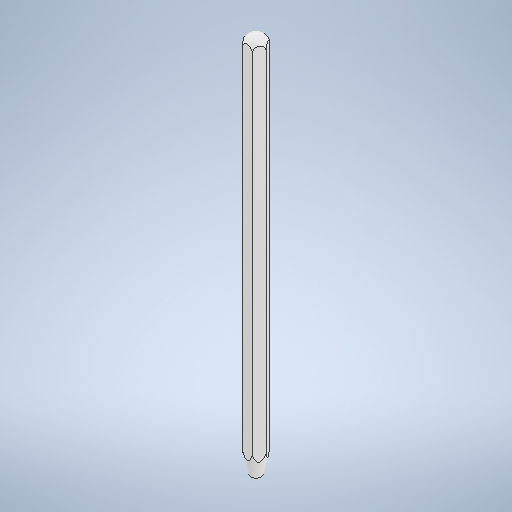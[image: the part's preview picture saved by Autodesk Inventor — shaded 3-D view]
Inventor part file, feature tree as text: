
AUTODESK INVENTOR PART (.ipt)
format: ipt  version: 2025.1 (Build 291241000, 241)  size: 307,200 bytes
history: native  units: mm
features: thicken_offset x6, sketch x5, revolve x3, extrude x2
ambient origin geometry x8: Origin, YZ Plane, XZ Plane, XY Plane, X Axis, Y Axis, Z Axis, Center Point
bodies: Solid1 (feature_tree)
feature tree (16):
  extrude  "Extrusion1"  Depth=155.0mm TaperAngle=0.0deg
  revolve  "Revolution1"  [1 undecoded]
  extrude  "Extrusion2"  Depth=10.0mm
  revolve  "Revolution2"  [1 undecoded]
  thicken_offset  "Thicken1"
  thicken_offset  "Thicken2"
  thicken_offset  "Thicken3"
  thicken_offset  "Thicken4"
  thicken_offset  "Thicken5"
  thicken_offset  "Thicken6"
  revolve  "Revolution3"  [1 undecoded]
  sketch  "Sketch1"  dims[d1=9.0mm d2=155.0mm d3=0.0mm]
  sketch  "Sketch2"  dims[d4=90.0deg d5=400.0mm d6=0.0mm]
  sketch  "Sketch3"  dims[d7=10.0mm d9=2.5mm]
  sketch  "Sketch4"  dims[d10=90.0deg d11=5.0mm]
  sketch  "Sketch5"  dims[d12=5.0mm d13=5.0mm d14=5.0mm d15=5.0mm d16=5.0mm d17=5.0mm d18=5.0mm d19=5.0mm d20=5.0mm d21=5.0mm d22=5.0mm d23=4.0mm d24=90.0deg]
note: 3 required parameter values undecoded (feature->parameter linkage not recoverable at this tier; creation-order binding heuristic only, values carry confidence <= 0.55)
